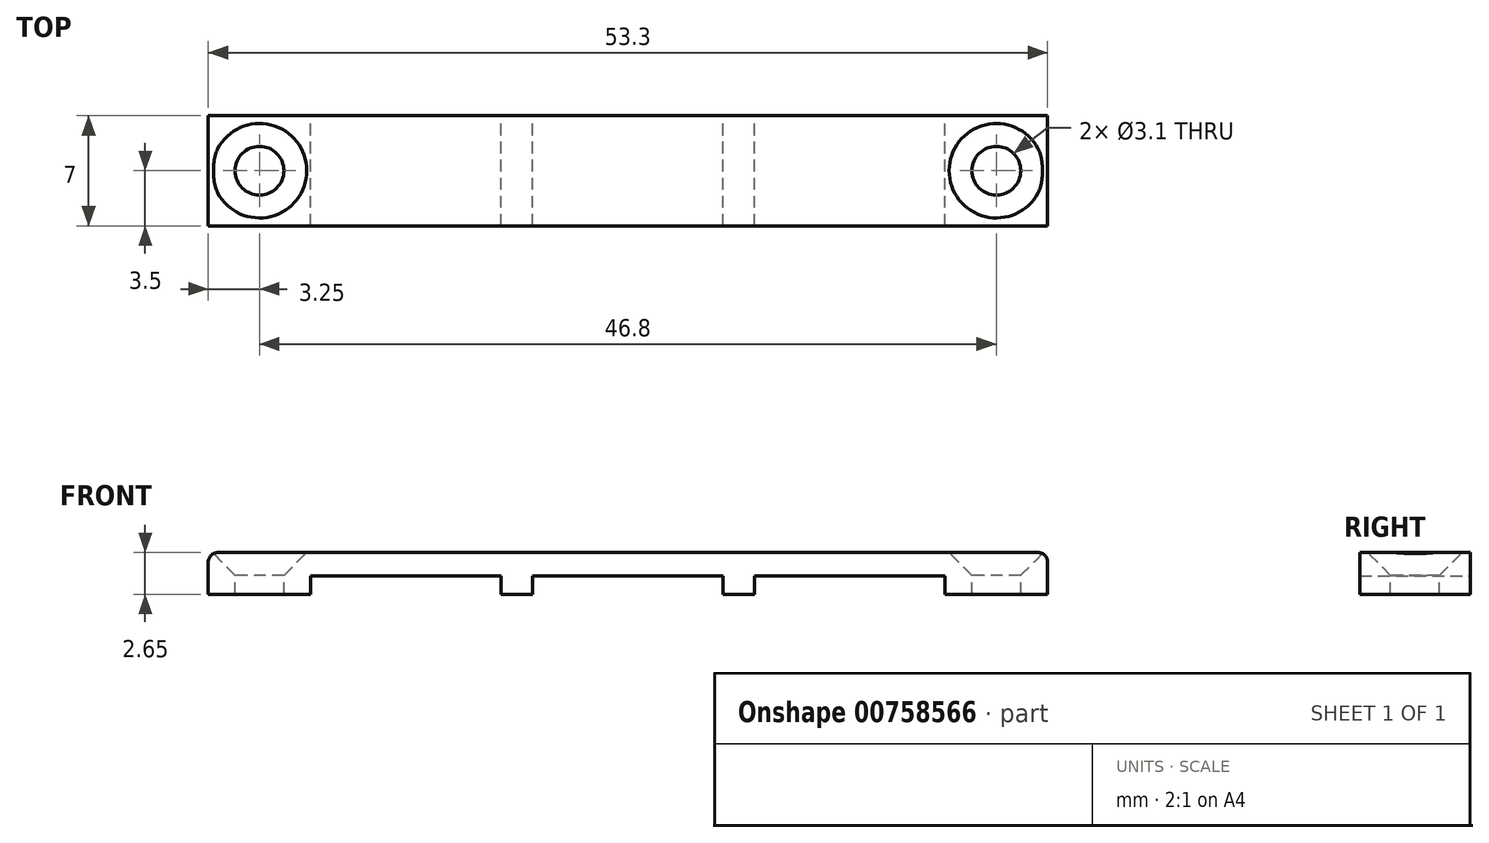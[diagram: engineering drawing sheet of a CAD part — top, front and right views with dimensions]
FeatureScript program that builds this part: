
annotation { "Feature Type Name" : "Feature", "Feature Type Description" : "" }
export const myFeature = defineFeature(function(context is Context, id is Id, definition is map)
    precondition{}
    {
        {
            assignVariable(context, id + "F0", {"name" : "clipwidht", "anyValue" : 7});
        }
        {
            var Q0;
            Q0=qCreatedBy(makeId("Front.planeOp"),FACE);
            var sketch = newSketch(context, id + "F1", { "sketchPlane" : qUnion([Q0])});
            skLineSegment(sketch, "E0", {"start": v(0, 1.15) * mm, "end": v(-6.05, 1.15) * mm});
            skLineSegment(sketch, "E1", {"start": v(-6.05, 1.15) * mm, "end": v(-6.05, 0) * mm});
            skLineSegment(sketch, "E2", {"start": v(-6.05, 0) * mm, "end": v(-8.05, 0) * mm});
            skLineSegment(sketch, "E3", {"start": v(-8.05, 0) * mm, "end": v(-8.05, 1.15) * mm});
            skLineSegment(sketch, "E4", {"start": v(-8.05, 1.15) * mm, "end": v(-20.15, 1.15) * mm});
            skLineSegment(sketch, "E5", {"start": v(-20.15, 1.15) * mm, "end": v(-20.15, 0) * mm});
            skLineSegment(sketch, "E6", {"start": v(-26.05, 2.65) * mm, "end": v(0, 2.65) * mm});
            skLineSegment(sketch, "E7", {"start": v(-26.65, 2.05) * mm, "end": v(-26.65, 0) * mm});
            skLineSegment(sketch, "E8", {"start": v(-26.65, 0) * mm, "end": v(-20.15, 0) * mm});
            skPoint(sketch, "E9.visualSharp", {"position": v(-26.65, 2.65) * mm});
            skArc(sketch, "E9.filletArc", {"start": v(-26.05, 2.65) * mm, "mid": v(-26.47, 2.47) * mm, "end": v(-26.65, 2.05) * mm});
            skArc(sketch, "E10.MirrorCS", {"start": v(26.05, 2.65) * mm, "mid": v(26.47, 2.47) * mm, "end": v(26.65, 2.05) * mm});
            skLineSegment(sketch, "E11.MirrorCS", {"start": v(8.05, 0) * mm, "end": v(8.05, 1.15) * mm});
            skLineSegment(sketch, "E12.MirrorCS", {"start": v(8.05, 1.15) * mm, "end": v(20.15, 1.15) * mm});
            skLineSegment(sketch, "E13.MirrorCS", {"start": v(26.65, 0) * mm, "end": v(20.15, 0) * mm});
            skPoint(sketch, "E14.MirrorP", {"position": v(26.65, 2.65) * mm});
            skLineSegment(sketch, "E15.MirrorCS", {"start": v(20.15, 1.15) * mm, "end": v(20.15, 0) * mm});
            skLineSegment(sketch, "E16.MirrorCS", {"start": v(26.65, 2.05) * mm, "end": v(26.65, 0) * mm});
            skLineSegment(sketch, "E17.MirrorCS", {"start": v(6.05, 0) * mm, "end": v(8.05, 0) * mm});
            skLineSegment(sketch, "E18.MirrorCS", {"start": v(6.05, 1.15) * mm, "end": v(6.05, 0) * mm});
            skLineSegment(sketch, "E19.MirrorCS", {"start": v(0, 1.15) * mm, "end": v(6.05, 1.15) * mm});
            skLineSegment(sketch, "E20.MirrorCS", {"start": v(26.05, 2.65) * mm, "end": v(0, 2.65) * mm});
            skSolve(sketch);
        }
        {
            var Q0;
            Q0=makeQuery(id+"F1.imprint","IMPRINT",FACE,{"disambiguationData":[TD([[makeQuery(id+"F1.imprint","IMPRINT",EDGE,{"derivedFrom":sQuery(id+"F1.wireOp",EDGE,"E0")}),-1.0]])]});
            extrude(context, id + "F2", {"entities" : qUnion([Q0]), "depth" : (getVariable(context, 'clipwidht')) * mm, "offsetDistance" : 25 * mm});
        }
        {
            var Q0;
            Q0=makeQuery(id+"F2.opExtrude","SWEPT_FACE",FACE,{"disambiguationData":[OSD([sQuery(id+"F1.wireOp",EDGE,"E8")])]});
            var sketch = newSketch(context, id + "F3", { "sketchPlane" : qUnion([Q0])});
            skLineSegment(sketch, "E21", {"start": v(-23.4, 7) * mm, "end": v(-23.4, 0) * mm, "construction": true});
            skLineSegment(sketch, "E22", {"start": v(-26.65, 3.5) * mm, "end": v(-20.15, 3.5) * mm, "construction": true});
            skPoint(sketch, "E23", {"position": v(-23.4, 3.5) * mm});
            skLineSegment(sketch, "E24", {"start": v(-23.4, 5.02) * mm, "end": v(-23.4, 4.96) * mm});
            skLineSegment(sketch, "E25", {"start": v(-22.68, 3.5) * mm, "end": v(-22.6, 3.5) * mm});
            skSolve(sketch);
        }
        {
            var Q0;
            Q0=makeQuery(id+"F2.opExtrude","SWEPT_FACE",FACE,{"disambiguationData":[OSD([sQuery(id+"F1.wireOp",EDGE,"E6"),sQuery(id+"F1.wireOp",EDGE,"E20.MirrorCS")])]});
            var sketch = newSketch(context, id + "F4", { "sketchPlane" : qUnion([Q0])});
            skPoint(sketch, "E26.0", {"position": v(-23.4, -3.5) * mm});
            skLineSegment(sketch, "E27", {"start": v(0, 0) * mm, "end": v(0, -7) * mm});
            skPoint(sketch, "E28.MirrorP", {"position": v(23.4, -3.5) * mm});
            skSolve(sketch);
        }
        {
            var Q0;
            Q0=sQuery(id+"F4.wireOp",VERTEX,"E26.0");
            var Q1;
            Q1=makeQuery(id+"F2.opExtrude","SWEPT_BODY",BODY,{"disambiguationData":[OSD([sQuery(id+"F1.wireOp",EDGE,"E0"),sQuery(id+"F1.wireOp",EDGE,"E1"),sQuery(id+"F1.wireOp",EDGE,"E2"),sQuery(id+"F1.wireOp",EDGE,"E3"),sQuery(id+"F1.wireOp",EDGE,"E4"),sQuery(id+"F1.wireOp",EDGE,"E5"),sQuery(id+"F1.wireOp",EDGE,"E6"),sQuery(id+"F1.wireOp",EDGE,"E7"),sQuery(id+"F1.wireOp",EDGE,"E8"),sQuery(id+"F1.wireOp",EDGE,"E9.filletArc"),sQuery(id+"F1.wireOp",EDGE,"E10.MirrorCS"),sQuery(id+"F1.wireOp",EDGE,"E11.MirrorCS"),sQuery(id+"F1.wireOp",EDGE,"E12.MirrorCS"),sQuery(id+"F1.wireOp",EDGE,"E13.MirrorCS"),sQuery(id+"F1.wireOp",EDGE,"E15.MirrorCS"),sQuery(id+"F1.wireOp",EDGE,"E16.MirrorCS"),sQuery(id+"F1.wireOp",EDGE,"E17.MirrorCS"),sQuery(id+"F1.wireOp",EDGE,"E18.MirrorCS"),sQuery(id+"F1.wireOp",EDGE,"E19.MirrorCS"),sQuery(id+"F1.wireOp",EDGE,"E20.MirrorCS")])]});
            hole(context, id + "F5", {"style" : HoleStyle.C_SINK, "endStyle" : HoleEndStyle.THROUGH, "holeDiameter" : 3.1 * mm, "cSinkDiameter" : 6 * mm, "cSinkAngle" : 90 * degree, "majorDiameter" : 3 * mm, "isTappedThrough" : true, "tappedDepth" : 12 * mm, "tapClearance" : 3, "startFromSketch" : true, "locations" : qUnion([Q0]), "scope" : qUnion([Q1])});
        }
        {
            var Q0;
            Q0=sQuery(id+"F4.wireOp",VERTEX,"E28.MirrorP");
            var Q1;
            Q1=makeQuery(id+"F2.opExtrude","SWEPT_BODY",BODY,{"disambiguationData":[OSD([sQuery(id+"F1.wireOp",EDGE,"E0"),sQuery(id+"F1.wireOp",EDGE,"E1"),sQuery(id+"F1.wireOp",EDGE,"E2"),sQuery(id+"F1.wireOp",EDGE,"E3"),sQuery(id+"F1.wireOp",EDGE,"E4"),sQuery(id+"F1.wireOp",EDGE,"E5"),sQuery(id+"F1.wireOp",EDGE,"E6"),sQuery(id+"F1.wireOp",EDGE,"E7"),sQuery(id+"F1.wireOp",EDGE,"E8"),sQuery(id+"F1.wireOp",EDGE,"E9.filletArc"),sQuery(id+"F1.wireOp",EDGE,"E10.MirrorCS"),sQuery(id+"F1.wireOp",EDGE,"E11.MirrorCS"),sQuery(id+"F1.wireOp",EDGE,"E12.MirrorCS"),sQuery(id+"F1.wireOp",EDGE,"E13.MirrorCS"),sQuery(id+"F1.wireOp",EDGE,"E15.MirrorCS"),sQuery(id+"F1.wireOp",EDGE,"E16.MirrorCS"),sQuery(id+"F1.wireOp",EDGE,"E17.MirrorCS"),sQuery(id+"F1.wireOp",EDGE,"E18.MirrorCS"),sQuery(id+"F1.wireOp",EDGE,"E19.MirrorCS"),sQuery(id+"F1.wireOp",EDGE,"E20.MirrorCS")])]});
            hole(context, id + "F6", {"style" : HoleStyle.C_SINK, "endStyle" : HoleEndStyle.THROUGH, "holeDiameter" : 3.1 * mm, "cSinkDiameter" : 6 * mm, "cSinkAngle" : 90 * degree, "majorDiameter" : 5 * mm, "isTappedThrough" : true, "tappedDepth" : 12 * mm, "tapClearance" : 3, "startFromSketch" : true, "locations" : qUnion([Q0]), "scope" : qUnion([Q1])});
        }
    });
